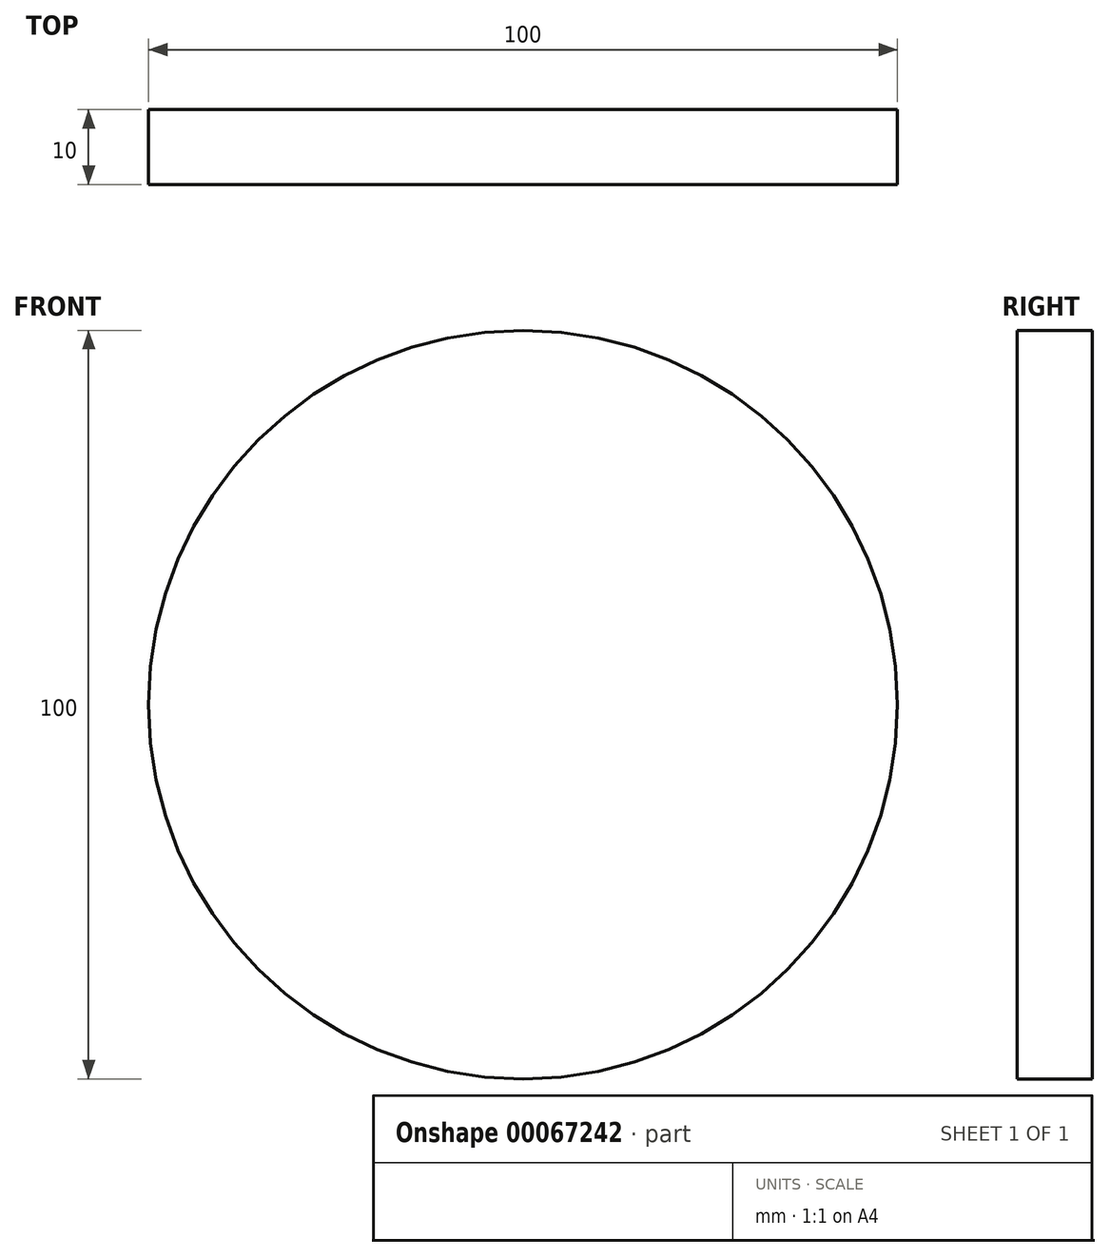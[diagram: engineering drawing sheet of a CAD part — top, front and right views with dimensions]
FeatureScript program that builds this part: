
annotation { "Feature Type Name" : "Feature", "Feature Type Description" : "" }
export const myFeature = defineFeature(function(context is Context, id is Id, definition is map)
    precondition{}
    {
        {
            var Q0;
            Q0=qCreatedBy(makeId("Front.planeOp"),FACE);
            var sketch = newSketch(context, id + "F0", { "sketchPlane" : qUnion([Q0])});
            skCircle(sketch, "E0", {"center": v(0, 0) * mm, "radius": 50 * mm});
            skSolve(sketch);
        }
        {
            var Q0;
            Q0 = qSketchRegion(id + "F0", true);
            extrude(context, id + "F1", {"entities" : qUnion([Q0]), "endBound" : BoundingType.SYMMETRIC, "depth" : 10 * mm});
        }
    });
